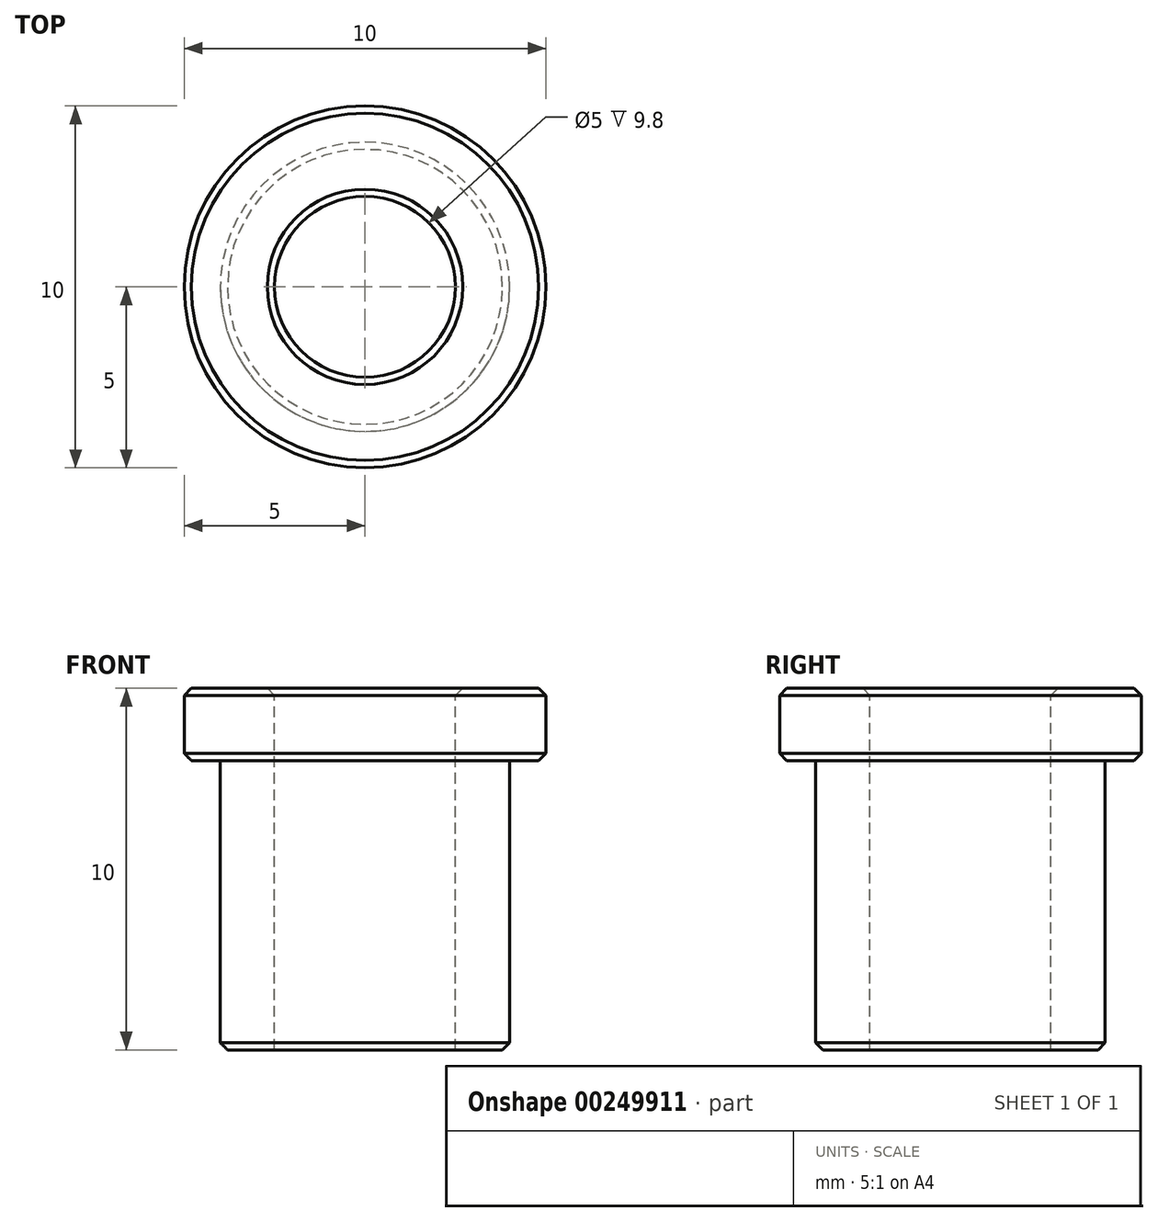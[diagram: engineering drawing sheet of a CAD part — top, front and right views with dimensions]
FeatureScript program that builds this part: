
annotation { "Feature Type Name" : "Feature", "Feature Type Description" : "" }
export const myFeature = defineFeature(function(context is Context, id is Id, definition is map)
    precondition{}
    {
        {
            var Q0;
            Q0=qCreatedBy(makeId("Front.planeOp"),FACE);
            var sketch = newSketch(context, id + "F0", { "sketchPlane" : qUnion([Q0])});
            skLineSegment(sketch, "E0", {"start": v(0, 10) * mm, "end": v(-2.5, 10) * mm});
            skLineSegment(sketch, "E1", {"start": v(-2.5, 10) * mm, "end": v(-2.5, 8) * mm});
            skLineSegment(sketch, "E2", {"start": v(-2.5, 8) * mm, "end": v(-1.5, 8) * mm});
            skLineSegment(sketch, "E3", {"start": v(-1.5, 8) * mm, "end": v(-1.5, 0) * mm});
            skLineSegment(sketch, "E4", {"start": v(-1.5, 0) * mm, "end": v(0, 0) * mm});
            skLineSegment(sketch, "E5", {"start": v(0, 0) * mm, "end": v(0, 10) * mm});
            skLineSegment(sketch, "E6", {"start": v(2.5, 10.98) * mm, "end": v(2.5, -2.88) * mm, "construction": true});
            skSolve(sketch);
        }
        {
            var Q0;
            Q0 = qSketchRegion(id + "F0", true);
            var Q1;
            Q1=sQuery(id+"F0.wireOp",EDGE,"E6");
            revolve(context, id + "F1", {"entities" : qUnion([Q0]), "axis" : qUnion([Q1]), "revolveType" : RevolveType.FULL});
        }
        {
            var Q0;
            Q0=makeQuery(id+"F1.opRevolve","SWEPT_EDGE",EDGE,{"disambiguationData":[OSD([sQuery(id+"F0.wireOp",EDGE,"E0"),sQuery(id+"F0.wireOp",EDGE,"E5")])]});
            var Q1;
            Q1=makeQuery(id+"F1.opRevolve","SWEPT_EDGE",EDGE,{"disambiguationData":[OSD([sQuery(id+"F0.wireOp",EDGE,"E0"),sQuery(id+"F0.wireOp",EDGE,"E1")])]});
            chamfer(context, id + "F2", {"entities" : qUnion([Q0, Q1]), "width" : .2 * mm, "tangentPropagation" : true});
        }
        {
            var Q0;
            Q0=makeQuery(id+"F1.opRevolve","SWEPT_EDGE",EDGE,{"disambiguationData":[OSD([sQuery(id+"F0.wireOp",EDGE,"E1"),sQuery(id+"F0.wireOp",EDGE,"E2")])]});
            var Q1;
            Q1=makeQuery(id+"F1.opRevolve","SWEPT_EDGE",EDGE,{"disambiguationData":[OSD([sQuery(id+"F0.wireOp",EDGE,"E3"),sQuery(id+"F0.wireOp",EDGE,"E4")])]});
            chamfer(context, id + "F3", {"entities" : qUnion([Q0, Q1]), "width" : .2 * mm, "tangentPropagation" : true});
        }
    });
